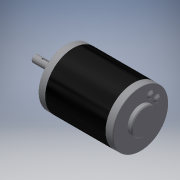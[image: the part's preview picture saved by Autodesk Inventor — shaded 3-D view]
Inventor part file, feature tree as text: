
AUTODESK INVENTOR PART (.ipt)
format: ipt  version: 2019 (Build 230136000, 136)  size: 163,328 bytes
history: native  units: in
note: dims shown in document units (in); Inventor stores cm internally (conversion verified against a paired STEP export)
features: chamfer x1
ambient origin geometry x8: Origin, YZ Plane, XZ Plane, XY Plane, X Axis, Y Axis, Z Axis, Center Point
bodies: Solid1 (feature_tree)
feature tree (1):
  chamfer  "Chamfer3"  [1 undecoded]
note: 1 required parameter value undecoded (feature->parameter linkage not recoverable at this tier; creation-order binding heuristic only, values carry confidence <= 0.55)
